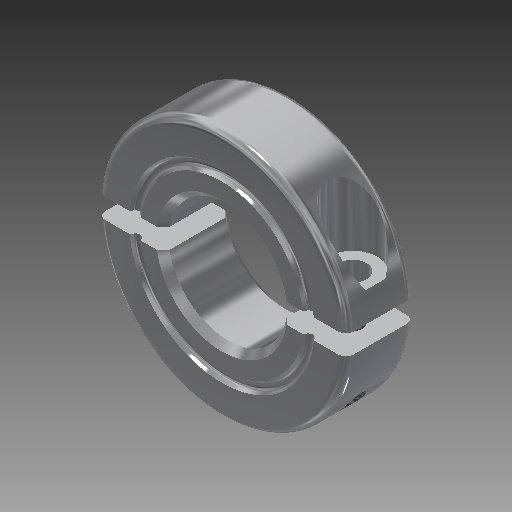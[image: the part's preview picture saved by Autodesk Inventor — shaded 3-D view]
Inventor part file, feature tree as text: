
AUTODESK INVENTOR PART (.ipt)
format: ipt  version: 2018 (Build 220112000, 112)  size: 318,976 bytes
history: native  units: in
note: dims shown in document units (in); Inventor stores cm internally (conversion verified against a paired STEP export)
features: thread x2, imported_body x2, other x1
ambient origin geometry x8: Origin, YZ Plane, XZ Plane, XY Plane, X Axis, Y Axis, Z Axis, Center Point
bodies: Solid1 (feature_tree), Solid2 (feature_tree)
feature tree (5):
  other  "ENSP20-6-A1"
  thread  "Thread1"  [1 undecoded]
  thread  "Thread2"  [1 undecoded]
  imported_body  "Base1"
  imported_body  "Base2"
note: 2 required parameter values undecoded (feature->parameter linkage not recoverable at this tier; creation-order binding heuristic only, values carry confidence <= 0.55)
